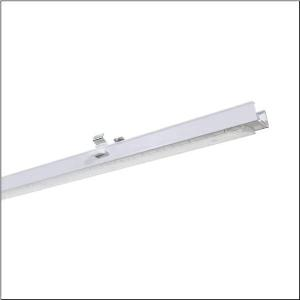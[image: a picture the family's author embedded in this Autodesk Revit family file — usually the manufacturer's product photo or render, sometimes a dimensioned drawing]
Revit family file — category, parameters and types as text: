
# Revit family: trunking_flex_31_51re19mb4cb
name_source: partatom
category: Lighting Fixtures
units: mm (PartAtom-declared; Revit-internal decimal feet)

## family parameters
Cut with Voids When Loaded = No
Host = Face
Light Source = No
Part Type = Normal
Room Calculation Point = No
Round Connector Dimension = Use Diameter
Shared = No

## types (1)
- --- (1 x LED, 11500 lm, 66 W, 4000K)
    Apparent Load = 66 VA
    CIE Flux Codes = 66 89 98 99 100
    Color Rendering = 80
    Color Temperature = 4000K
    Default Elevation = 1800 mm
    Description = Trunking Flex 31, luminaire insert, of extruded aluminium section, coated, traffic white (RAL 9016), length: 1.472mm, width: 91mm, height: 53mm, LED rated luminous flux: 11.500lm, light colour: 840, control gear: ON/OFF Multilumen, with system connector: socket, mains connection: 220..240V, AC, 50/60Hz, rated input power: 66W, connected load according to luminous flux setting (19/24/32/37/47/52/60/66W), luminous flux adjustable on luminaire in eight steps (3450/4380/5800/6700/8350/9200/10500/11500lm ), primary light control with lens, of plastic, primary optical cover: cover, of PMMA, light emission: direct distribution, primary light characteristic: double asymmetric, protection rating (complete): IP20, insulation class (complete): insulation class I (protective earthing), certification: CE, UKCA, impact resistance: IK02, permissible ambient temperature for indoor applications: -20..+40°C, packaging unit: 1 piece
    Height = 58 mm
    Lamp = 1 x LED
    Lamp Light Flux = 11500 lm
    Lamp Power = 66 W
    Lamp count = 1
    Length = 1472 mm
    Luminous efficacy = 174 lm/W
    Manufacturer = Siteco
    ModVariant = No
    Model = 51RE19MB4CB
    Mounting Place = Ceiling
    Mounting Type = Pendant
    Number of Poles = 1
    OnlyDefault = Yes
    Power Factor = 1
    Product Name = Trunking Flex 31
    Product group = luminaire insert
    ProductGroupID = 901
    Protection Class = Protection class I
    Protection Degree = IP 20
    RLX_Detail_Level = 1
    RLX_Emergency_Light_Flux = 0 lm
    RLX_Emergency_Type = 0
    RLX_Emergency_Type_DB = No
    RlxData = <blob elided: 21169 chars, md5=ba714fd2>
    Socket = socket
    Standby Power = 0 W
    System Light Flux = 11500 lm
    System Power = 66 W
    Type Comments = factory setting: luminous flux: 100 % | (ON | ON | ON)
    Type Image = l_1266702.jpg
    URL = http://relux.com
    VarID = @adj_027195
    Voltage = 0 V
    Weight = 0.00 kg
    Width = 65 mm

## geometry (parser evidence)
native form markers: Blend x4, Sweep x12
no freeform markers — native parametric forms only
